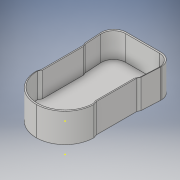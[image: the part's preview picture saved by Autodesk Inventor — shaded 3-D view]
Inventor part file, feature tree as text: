
AUTODESK INVENTOR PART (.ipt)
format: ipt  version: 2018 (Build 220112000, 112)  size: 197,120 bytes
history: native  units: in
note: dims shown in document units (in); Inventor stores cm internally (conversion verified against a paired STEP export)
features: sketch x9, extrude x2, plane x2
ambient origin geometry x8: Origin, YZ Plane, XZ Plane, XY Plane, X Axis, Y Axis, Z Axis, Center Point
bodies: Solid1 (feature_tree)
feature tree (13):
  sketch  "Sketch1"  dims[d2=1.162in d3=0.0in d5=1.1591in]
  extrude  "Extrusion1"  Depth=1.1591in
  extrude  "Extrusion2"  Depth=0.8in
  sketch  "Sketch4"  dims[d9=1.124in d10=1.5753in d11=0.776in d12=0.485in]
  sketch  "Sketch5"  dims[d13=1.0in d14=0.0in]
  sketch  "Sketch6"  dims[d15=90.0deg]
  plane  "Work Plane3"
  sketch  "Sketch7"
  sketch  "Sketch8"
  plane  "Work Plane4"
  sketch  "Sketch9"
  sketch  "Sketch2"  dims[d6=1.624in d7=0.8in]
  sketch  "Sketch3"  dims[d8=0.5in]
